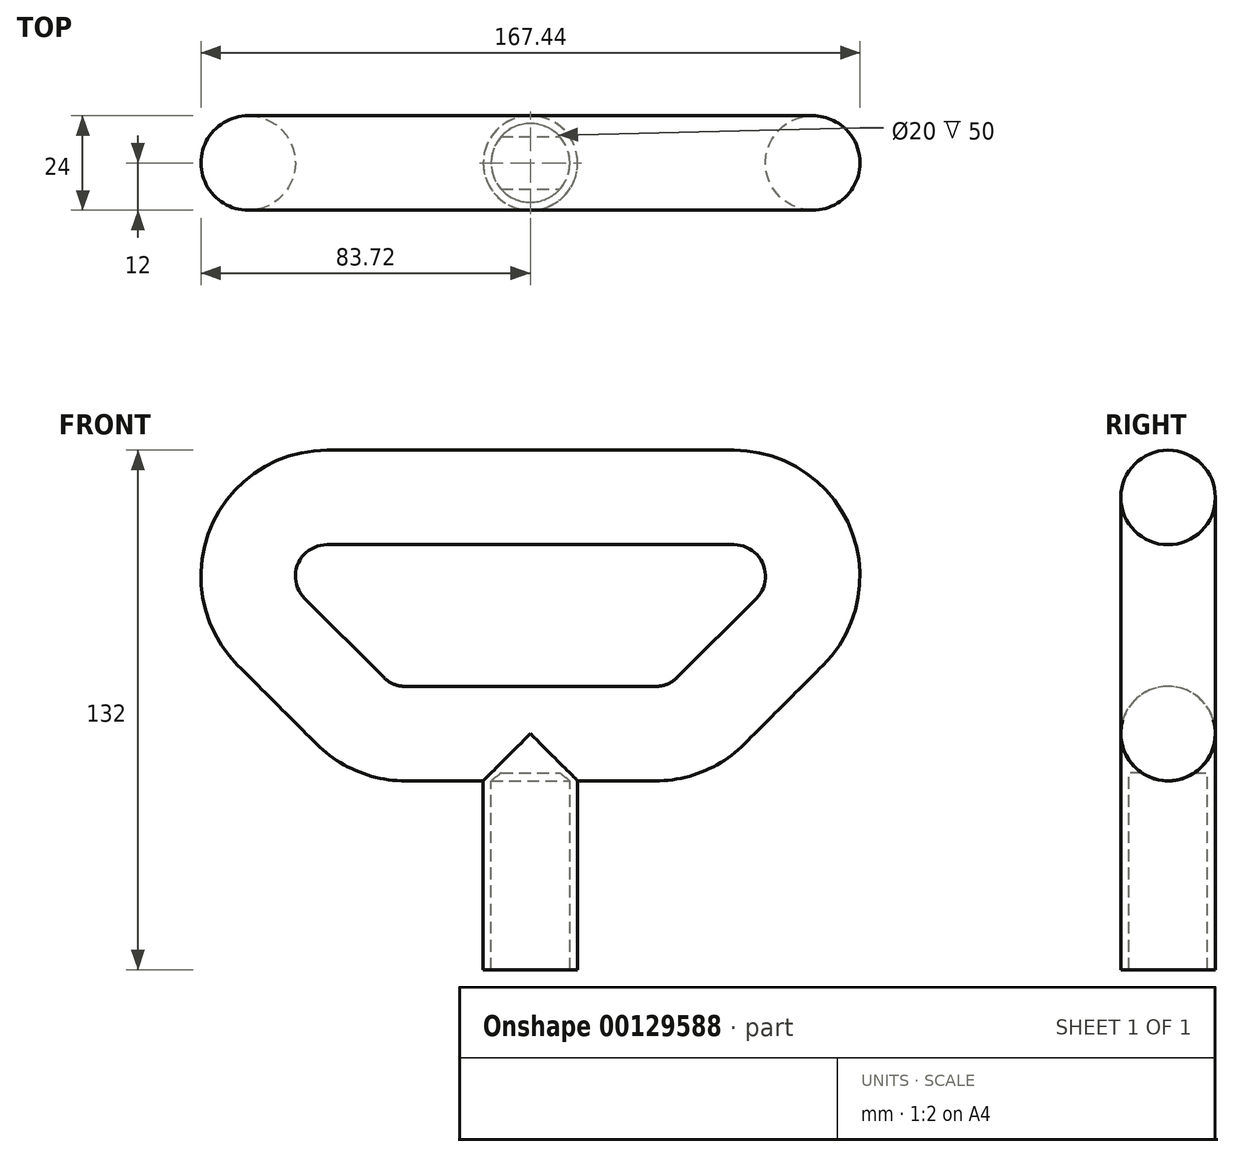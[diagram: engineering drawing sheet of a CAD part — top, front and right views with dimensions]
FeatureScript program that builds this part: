
annotation { "Feature Type Name" : "Feature", "Feature Type Description" : "" }
export const myFeature = defineFeature(function(context is Context, id is Id, definition is map)
    precondition{}
    {
        {
            var Q0;
            Q0=qCreatedBy(makeId("Front.planeOp"),FACE);
            var sketch = newSketch(context, id + "F0", { "sketchPlane" : qUnion([Q0])});
            skLineSegment(sketch, "E0.bottom", {"start": v(-10, 0) * mm, "end": v(-12, 0) * mm});
            skLineSegment(sketch, "E0.top", {"start": v(0, 60) * mm, "end": v(-12, 60) * mm});
            skLineSegment(sketch, "E0.left", {"start": v(0, 50) * mm, "end": v(0, 60) * mm});
            skLineSegment(sketch, "E0.right", {"start": v(-12, 0) * mm, "end": v(-12, 60) * mm});
            skLineSegment(sketch, "E1.1", {"start": v(0, 50) * mm, "end": v(-10, 50) * mm});
            skLineSegment(sketch, "E2", {"start": v(0, 50) * mm, "end": v(0, 0) * mm, "construction": true});
            skLineSegment(sketch, "E3", {"start": v(0, 0) * mm, "end": v(-10, 0) * mm, "construction": true});
            skLineSegment(sketch, "E4", {"start": v(-10, 50) * mm, "end": v(-10, 0) * mm});
            skSolve(sketch);
        }
        {
            var Q0;
            Q0 = qSketchRegion(id + "F0", true);
            var Q1;
            Q1=sQuery(id+"F0.wireOp",EDGE,"E2");
            revolve(context, id + "F1", {"entities" : qUnion([Q0]), "axis" : qUnion([Q1]), "revolveType" : RevolveType.FULL});
        }
        {
            var Q0;
            Q0=qCreatedBy(makeId("Front.planeOp"),FACE);
            var sketch = newSketch(context, id + "F2", { "sketchPlane" : qUnion([Q0])});
            skLineSegment(sketch, "E5", {"start": v(0, 60) * mm, "end": v(-31.72, 60) * mm});
            skLineSegment(sketch, "E6", {"start": v(-45.86, 65.86) * mm, "end": v(-65.86, 85.86) * mm});
            skLineSegment(sketch, "E7", {"start": v(-51.72, 120) * mm, "end": v(51.72, 120) * mm});
            skLineSegment(sketch, "E8", {"start": v(65.86, 85.86) * mm, "end": v(45.86, 65.86) * mm});
            skLineSegment(sketch, "E9", {"start": v(0, 120) * mm, "end": v(0, 60) * mm, "construction": true});
            skPoint(sketch, "E10.visualSharp", {"position": v(-100, 120) * mm});
            skArc(sketch, "E10.filletArc", {"start": v(-51.72, 120) * mm, "mid": v(-70.2, 107.65) * mm, "end": v(-65.86, 85.86) * mm});
            skPoint(sketch, "E11.visualSharp", {"position": v(100, 120) * mm});
            skArc(sketch, "E11.filletArc", {"start": v(65.86, 85.86) * mm, "mid": v(70.2, 107.65) * mm, "end": v(51.72, 120) * mm});
            skPoint(sketch, "E12.visualSharp", {"position": v(40, 60) * mm});
            skArc(sketch, "E12.filletArc", {"start": v(31.72, 60) * mm, "mid": v(39.37, 61.52) * mm, "end": v(45.86, 65.86) * mm});
            skPoint(sketch, "E13.visualSharp", {"position": v(-40, 60) * mm});
            skArc(sketch, "E13.filletArc", {"start": v(-45.86, 65.86) * mm, "mid": v(-39.37, 61.52) * mm, "end": v(-31.72, 60) * mm});
            skLineSegment(sketch, "E14", {"start": v(0, 60) * mm, "end": v(31.72, 60) * mm});
            skSolve(sketch);
        }
        {
            var Q0;
            Q0=qCreatedBy(makeId("Right.planeOp"),FACE);
            var sketch = newSketch(context, id + "F3", { "sketchPlane" : qUnion([Q0])});
            skCircle(sketch, "E15", {"center": v(0, 60) * mm, "radius": 12 * mm});
            skSolve(sketch);
        }
        {
            var Q0;
            Q0 = qSketchRegion(id + "F3", true);
            var Q1;
            Q1=sQuery(id+"F2.wireOp",EDGE,"E5");
            var Q2;
            Q2=sQuery(id+"F2.wireOp",EDGE,"E13.filletArc");
            var Q3;
            Q3=sQuery(id+"F2.wireOp",EDGE,"E6");
            var Q4;
            Q4=sQuery(id+"F2.wireOp",EDGE,"E10.filletArc");
            var Q5;
            Q5=sQuery(id+"F2.wireOp",EDGE,"E7");
            var Q6;
            Q6=sQuery(id+"F2.wireOp",EDGE,"E11.filletArc");
            var Q7;
            Q7=sQuery(id+"F2.wireOp",EDGE,"E8");
            var Q8;
            Q8=sQuery(id+"F2.wireOp",EDGE,"E12.filletArc");
            var Q9;
            Q9=sQuery(id+"F2.wireOp",EDGE,"E14");
            sweep(context, id + "F4", {"operationType" : NewBodyOperationType.ADD, "profiles" : qUnion([Q0]), "path" : qUnion([Q1, Q2, Q3, Q4, Q5, Q6, Q7, Q8, Q9])});
        }
    });
